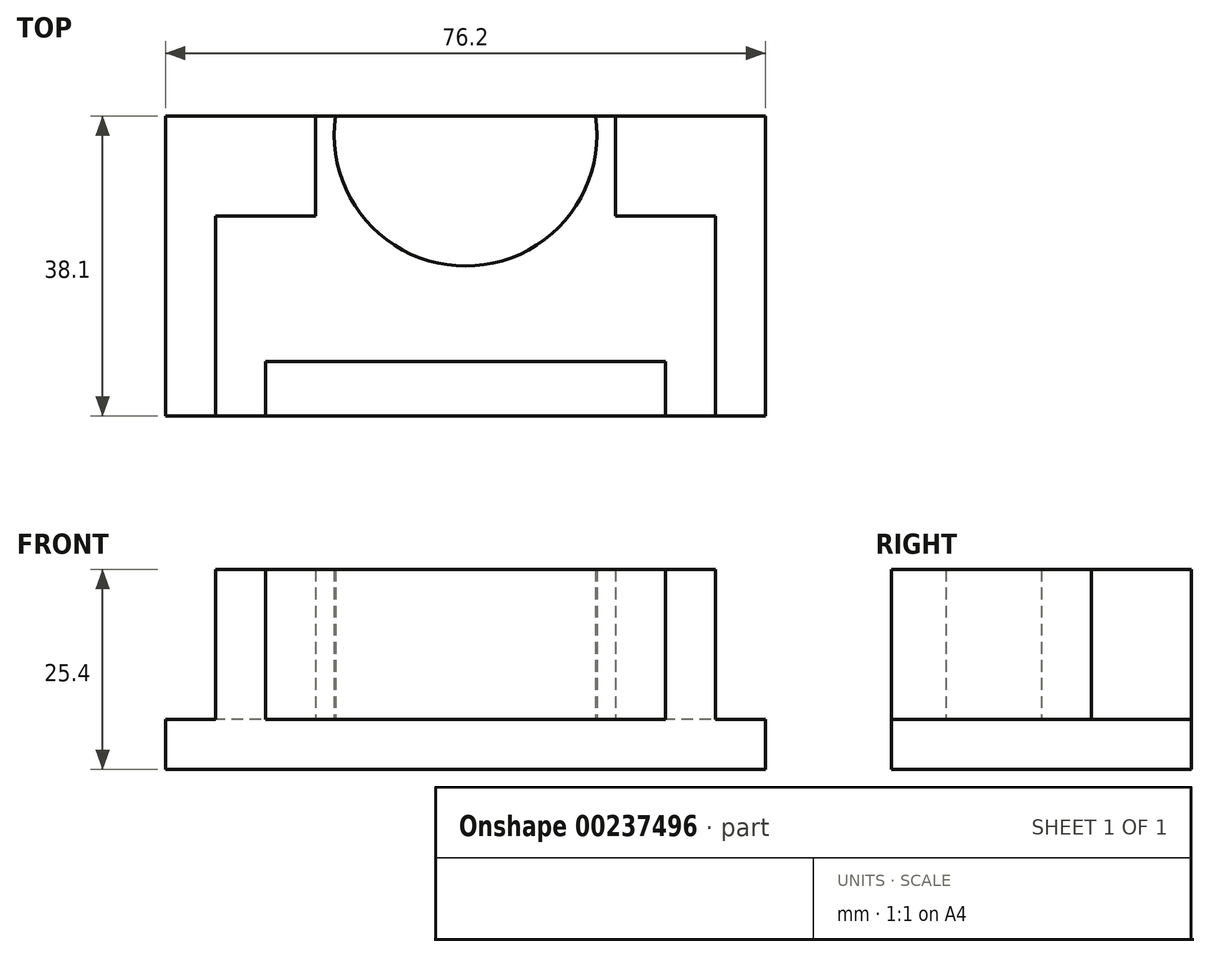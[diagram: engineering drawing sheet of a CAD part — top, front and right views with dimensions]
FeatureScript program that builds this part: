
annotation { "Feature Type Name" : "Feature", "Feature Type Description" : "" }
export const myFeature = defineFeature(function(context is Context, id is Id, definition is map)
    precondition{}
    {
        {
            var Q0;
            Q0=qCreatedBy(makeId("Top.planeOp"),FACE);
            var sketch = newSketch(context, id + "F0", { "sketchPlane" : qUnion([Q0])});
            skLineSegment(sketch, "E0.bottom", {"start": v(38.1, 19.05) * mm, "end": v(-38.1, 19.05) * mm});
            skLineSegment(sketch, "E0.top", {"start": v(38.1, -19.05) * mm, "end": v(-38.1, -19.05) * mm});
            skLineSegment(sketch, "E0.left", {"start": v(38.1, 19.05) * mm, "end": v(38.1, -19.05) * mm});
            skLineSegment(sketch, "E0.right", {"start": v(-38.1, 19.05) * mm, "end": v(-38.1, -19.05) * mm});
            skPoint(sketch, "E0.middle", {"position": v(0, 0) * mm});
            skSolve(sketch);
        }
        {
            var Q0;
            Q0=makeQuery(id+"F0.imprint","IMPRINT",FACE,{"disambiguationData":[TD([[makeQuery(id+"F0.imprint","IMPRINT",EDGE,{"derivedFrom":sQuery(id+"F0.wireOp",EDGE,"E0.bottom")}),1.0]])]});
            extrude(context, id + "F1", {"entities" : qUnion([Q0]), "depth" : 6.35 * mm});
        }
        {
            var Q0;
            Q0=makeQuery(id+"F1.opExtrude","CAP_FACE",FACE,{"disambiguationData":[OSD([sQuery(id+"F0.wireOp",EDGE,"E0.bottom"),sQuery(id+"F0.wireOp",EDGE,"E0.top"),sQuery(id+"F0.wireOp",EDGE,"E0.left"),sQuery(id+"F0.wireOp",EDGE,"E0.right")])],"isStart":false});
            var sketch = newSketch(context, id + "F2", { "sketchPlane" : qUnion([Q0])});
            skLineSegment(sketch, "E1.bottom", {"start": v(-31.75, 19.05) * mm, "end": v(31.75, 19.05) * mm});
            skLineSegment(sketch, "E1.top", {"start": v(-31.75, -19.05) * mm, "end": v(31.75, -19.05) * mm});
            skLineSegment(sketch, "E1.left", {"start": v(-31.75, 19.05) * mm, "end": v(-31.75, -19.05) * mm});
            skLineSegment(sketch, "E1.right", {"start": v(31.75, 19.05) * mm, "end": v(31.75, -19.05) * mm});
            skPoint(sketch, "E1.middle", {"position": v(0, 0) * mm});
            skSolve(sketch);
        }
        {
            var Q0;
            {var subQ0=sQuery(id+"F0.wireOp",EDGE,"E0.left");var subQ1=sQuery(id+"F0.wireOp",EDGE,"E0.top");var subQ2=sQuery(id+"F0.wireOp",EDGE,"E0.bottom");Q0=makeQuery(id+"FZAOSAdBaP8aMin_1.boolean.opBoolean","SPLIT",FACE,{"disambiguationData":[TD([makeQuery(id+"F1.opExtrude","SWEPT_FACE",FACE,{"disambiguationData":[OSD([subQ0])]})])],"derivedFrom":makeQuery(id+"F1.opExtrude","CAP_FACE",FACE,{"disambiguationData":[OSD([subQ2,subQ1,subQ0,sQuery(id+"F0.wireOp",EDGE,"E0.right")])],"isStart":false})});}
            var sketch = newSketch(context, id + "F3", { "sketchPlane" : qUnion([Q0])});
            skLineSegment(sketch, "E2.bottom", {"start": v(25.4, -12.16) * mm, "end": v(-25.4, -12.16) * mm});
            skLineSegment(sketch, "E2.top", {"start": v(25.4, -19.05) * mm, "end": v(-25.4, -19.05) * mm});
            skLineSegment(sketch, "E2.left", {"start": v(25.4, -12.16) * mm, "end": v(25.4, -19.05) * mm});
            skLineSegment(sketch, "E2.right", {"start": v(-25.4, -12.16) * mm, "end": v(-25.4, -19.05) * mm});
            skPoint(sketch, "E2.middle", {"position": v(0, -15.6) * mm});
            skPoint(sketch, "E3.third.point", {"position": v(0, 0) * mm});
            skLineSegment(sketch, "E4", {"start": v(-19.05, 19.06) * mm, "end": v(-16.5, 19.06) * mm});
            skLineSegment(sketch, "E5", {"start": v(19.05, 19.06) * mm, "end": v(16.51, 19.06) * mm});
            skArc(sketch, "E6", {"start": v(-16.51, 19.06) * mm, "mid": v(0, 0) * mm, "end": v(16.51, 19.06) * mm});
            skLineSegment(sketch, "E7", {"start": v(-19.05, 19.06) * mm, "end": v(-19.05, 6.36) * mm});
            skLineSegment(sketch, "E8", {"start": v(-19.05, 6.36) * mm, "end": v(-31.75, 6.36) * mm});
            skLineSegment(sketch, "E9", {"start": v(19.05, 19.06) * mm, "end": v(19.05, 6.36) * mm});
            skLineSegment(sketch, "E10", {"start": v(19.05, 6.36) * mm, "end": v(31.75, 6.36) * mm});
            skLineSegment(sketch, "E11", {"start": v(-38.1, 19.05) * mm, "end": v(-31.92, 19.05) * mm});
            skLineSegment(sketch, "E12", {"start": v(31.75, 6.36) * mm, "end": v(31.75, -19.05) * mm});
            skLineSegment(sketch, "E13", {"start": v(-31.75, 6.36) * mm, "end": v(-31.75, -19.05) * mm});
            skLineSegment(sketch, "E14", {"start": v(-31.75, -19.05) * mm, "end": v(-25.4, -19.05) * mm});
            skLineSegment(sketch, "E15", {"start": v(25.4, -19.05) * mm, "end": v(31.75, -19.05) * mm});
            skSolve(sketch);
        }
        {
            var Q0;
            Q0=makeQuery(id+"F3.imprint","IMPRINT",FACE,{"disambiguationData":[TD([[makeQuery(id+"F3.imprint","IMPRINT",EDGE,{"derivedFrom":sQuery(id+"F3.wireOp",EDGE,"E2.bottom")}),-1.0]])]});
            extrude(context, id + "F4", {"entities" : qUnion([Q0]), "operationType" : NewBodyOperationType.ADD, "depth" : 19.05 * mm});
        }
    });
